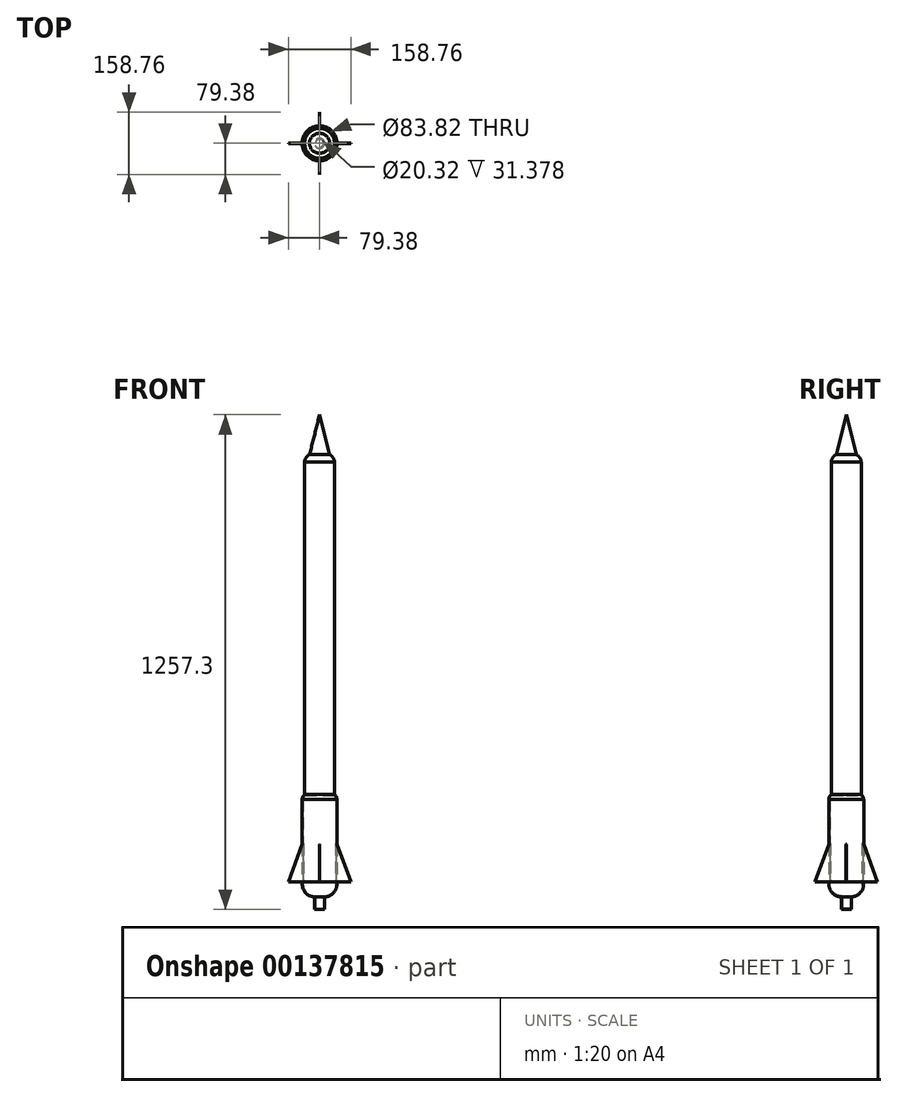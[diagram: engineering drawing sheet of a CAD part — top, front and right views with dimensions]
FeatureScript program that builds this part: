
annotation { "Feature Type Name" : "Feature", "Feature Type Description" : "" }
export const myFeature = defineFeature(function(context is Context, id is Id, definition is map)
    precondition{}
    {
        {
            var Q0;
            Q0=qCreatedBy(makeId("Front.planeOp"),FACE);
            var sketch = newSketch(context, id + "F0", { "sketchPlane" : qUnion([Q0])});
            skLineSegment(sketch, "E0", {"start": v(0, 0) * mm, "end": v(0, 1257.3) * mm});
            skLineSegment(sketch, "E1", {"start": v(0, 1257.3) * mm, "end": v(-25.4, 1155.7) * mm});
            skLineSegment(sketch, "E2", {"start": v(-38.1, 1136.65) * mm, "end": v(-38.1, 292.1) * mm});
            skFitSpline(sketch, "E3", {"points": [v(-25.4, 1155.7) * mm, v(-34.17, 1147.83) * mm, v(-38.1, 1136.65) * mm], "startDerivative": vector(-23.38, -6.73) * mm, "endDerivative": vector(-2.63, -30.67) * mm});
            skLineSegment(sketch, "E4", {"start": v(-25.4, 1155.7) * mm, "end": v(0, 1155.7) * mm});
            skLineSegment(sketch, "E5", {"start": v(0, 0) * mm, "end": v(-12.7, 0) * mm});
            skLineSegment(sketch, "E6", {"start": v(-12.7, 0) * mm, "end": v(-12.7, 31.75) * mm});
            skLineSegment(sketch, "E7", {"start": v(0, 292.1) * mm, "end": v(-38.1, 292.1) * mm});
            skLineSegment(sketch, "E8", {"start": v(-44.45, 279.8) * mm, "end": v(-44.45, 70.24) * mm});
            skFitSpline(sketch, "E9", {"points": [v(-38.1, 292.1) * mm, v(-41.91, 288.05) * mm, v(-44.45, 279.8) * mm], "startDerivative": vector(-9.45, -7.8) * mm, "endDerivative": vector(-3.47, -16.49) * mm});
            skFitSpline(sketch, "E10", {"points": [v(-44.45, 70.24) * mm, v(-41.3, 50.75) * mm, v(-27.55, 36.02) * mm, v(-12.7, 31.75) * mm], "startDerivative": vector(1.68, -58.21) * mm, "endDerivative": vector(49, -7.8) * mm});
            skSolve(sketch);
        }
        {
            var Q0;
            {var subQ0=sQuery(id+"F0.wireOp",EDGE,"E1");Q0=makeQuery(id+"F0.imprint","IMPRINT",FACE,{"disambiguationData":[TD([[makeQuery(id+"F0.imprint","IMPRINT",EDGE,{"derivedFrom":subQ0}),1.0]])]});}
            var Q1;
            Q1=sQuery(id+"F0.wireOp",EDGE,"E0");
            revolve(context, id + "F1", {"entities" : qUnion([Q0]), "axis" : qUnion([Q1]), "revolveType" : RevolveType.FULL});
        }
        {
            var Q0;
            Q0=makeQuery(id+"F0.imprint","IMPRINT",FACE,{"disambiguationData":[TD([[makeQuery(id+"F0.imprint","IMPRINT",EDGE,{"derivedFrom":sQuery(id+"F0.wireOp",EDGE,"E2")}),1.0]])]});
            var Q1;
            Q1=sQuery(id+"F0.wireOp",EDGE,"E0");
            revolve(context, id + "F2", {"entities" : qUnion([Q0]), "axis" : qUnion([Q1]), "revolveType" : RevolveType.FULL});
        }
        {
            var Q0;
            {var subQ0=sQuery(id+"F0.wireOp",EDGE,"E5");Q0=makeQuery(id+"F0.imprint","IMPRINT",FACE,{"disambiguationData":[TD([[makeQuery(id+"F0.imprint","IMPRINT",EDGE,{"derivedFrom":subQ0}),-1.0]])]});}
            var Q1;
            Q1=sQuery(id+"F0.wireOp",EDGE,"E0");
            revolve(context, id + "F3", {"entities" : qUnion([Q0]), "axis" : qUnion([Q1]), "revolveType" : RevolveType.FULL});
        }
        {
            var Q0;
            Q0=qCreatedBy(makeId("Right.planeOp"),FACE);
            var sketch = newSketch(context, id + "F4", { "sketchPlane" : qUnion([Q0])});
            skLineSegment(sketch, "E11.0", {"start": v(44.45, 70.24) * mm, "end": v(-44.45, 70.24) * mm, "construction": true});
            skLineSegment(sketch, "E12", {"start": v(44.45, 70.24) * mm, "end": v(79.37, 70.24) * mm});
            skLineSegment(sketch, "E13", {"start": v(79.38, 70.24) * mm, "end": v(44.45, 165.5) * mm});
            skLineSegment(sketch, "E14", {"start": v(44.45, 165.5) * mm, "end": v(44.45, 70.24) * mm});
            skLineSegment(sketch, "E15", {"start": v(44.45, 165.5) * mm, "end": v(40.2, 167.9) * mm});
            skLineSegment(sketch, "E16", {"start": v(40.2, 167.9) * mm, "end": v(40.2, 70.24) * mm});
            skLineSegment(sketch, "E17", {"start": v(40.2, 70.24) * mm, "end": v(44.45, 70.24) * mm});
            skSolve(sketch);
        }
        {
            var Q0;
            Q0 = qSketchRegion(id + "F4", true);
            var Q1;
            Q1=sQuery(id+"F4.wireOp",EDGE,"E12");
            extrude(context, id + "F5", {"entities" : qUnion([Q0]), "surfaceEntities" : qUnion([Q1]), "depth" : 0.95 * mm, "symmetric" : true});
        }
        {
            var Q0;
            Q0=makeQuery(id+"F3.opRevolve","SWEPT_FACE",FACE,{"disambiguationData":[OSD([sQuery(id+"F0.wireOp",EDGE,"E8")])]});
            var Q1;
            Q1=makeQuery(id+"F3.opRevolve","SWEPT_FACE",FACE,{"disambiguationData":[OSD([sQuery(id+"F0.wireOp",EDGE,"E10")])]});
            var Q2;
            Q2=makeQuery(id+"F3.opRevolve","SWEPT_FACE",FACE,{"disambiguationData":[OSD([sQuery(id+"F0.wireOp",EDGE,"E6")])]});
            var Q3;
            Q3=makeQuery(id+"F3.opRevolve","SWEPT_BODY",BODY,{"disambiguationData":[OSD([sQuery(id+"F0.wireOp",EDGE,"E0"),sQuery(id+"F0.wireOp",EDGE,"E5"),sQuery(id+"F0.wireOp",EDGE,"E6"),sQuery(id+"F0.wireOp",EDGE,"E7"),sQuery(id+"F0.wireOp",EDGE,"E8"),sQuery(id+"F0.wireOp",EDGE,"E9"),sQuery(id+"F0.wireOp",EDGE,"E10")])]});
            shell(context, id + "F6", {"isHollow" : true, "entities" : qUnion([Q0, Q1, Q2]), "parts" : qUnion([Q3]), "thickness" : 2.54 * mm});
        }
        {
            var Q0;
            Q0=makeQuery(id+"F5.opExtrude","SWEPT_BODY",BODY,{"disambiguationData":[OSD([sQuery(id+"F4.wireOp",EDGE,"E12"),sQuery(id+"F4.wireOp",EDGE,"E13"),sQuery(id+"F4.wireOp",EDGE,"E15"),sQuery(id+"F4.wireOp",EDGE,"E16"),sQuery(id+"F4.wireOp",EDGE,"E17")])]});
            var Q1;
            Q1=sQuery(id+"F0.wireOp",EDGE,"E0");
            circularPattern(context, id + "F7", {"entities" : qUnion([Q0]), "axis" : qUnion([Q1]), "angle" : 360 * degree, "instanceCount" : 4, "equalSpace" : true});
        }
    });
